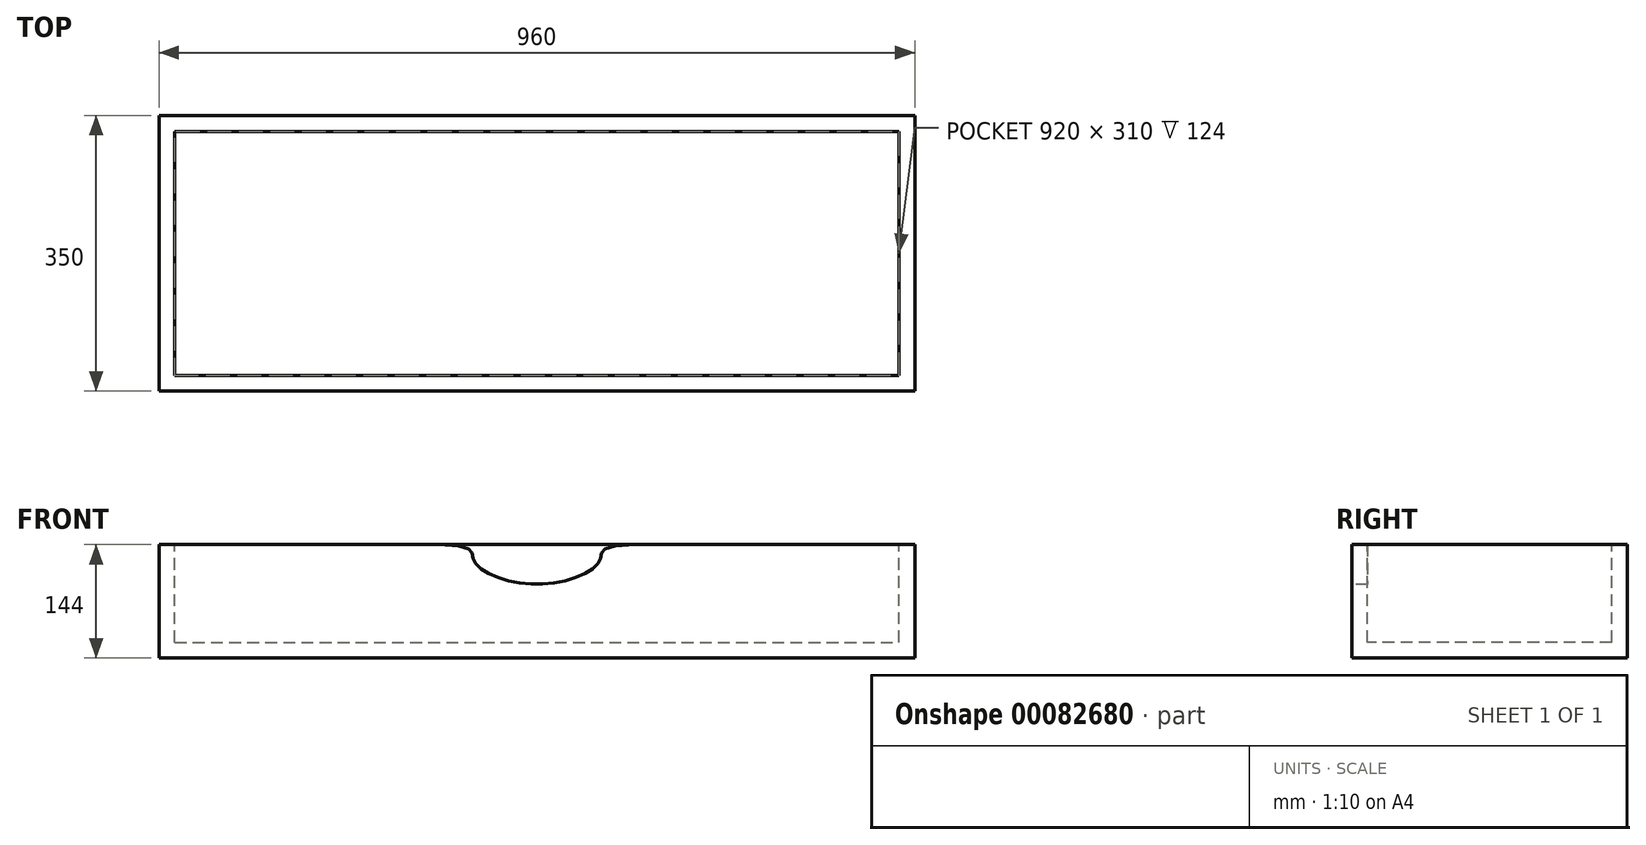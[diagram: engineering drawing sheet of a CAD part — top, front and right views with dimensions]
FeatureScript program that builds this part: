
annotation { "Feature Type Name" : "Feature", "Feature Type Description" : "" }
export const myFeature = defineFeature(function(context is Context, id is Id, definition is map)
    precondition{}
    {
        {
            var Q0;
            Q0=qCreatedBy(makeId("Top.planeOp"),FACE);
            var sketch = newSketch(context, id + "F0", { "sketchPlane" : qUnion([Q0])});
            skLineSegment(sketch, "E0.bottom", {"start": v(-480, 175) * mm, "end": v(480, 175) * mm});
            skLineSegment(sketch, "E0.top", {"start": v(-480, -175) * mm, "end": v(480, -175) * mm});
            skLineSegment(sketch, "E0.left", {"start": v(-480, 175) * mm, "end": v(-480, -175) * mm});
            skLineSegment(sketch, "E0.right", {"start": v(480, 175) * mm, "end": v(480, -175) * mm});
            skLineSegment(sketch, "E1", {"start": v(-480, 175) * mm, "end": v(480, -175) * mm, "construction": true});
            skSolve(sketch);
        }
        {
            var Q0;
            Q0 = qSketchRegion(id + "F0", true);
            extrude(context, id + "F1", {"entities" : qUnion([Q0]), "depth" : 144 * mm});
        }
        {
            var Q0;
            Q0=makeQuery(id+"F1.opExtrude","CAP_FACE",FACE,{"disambiguationData":[OSD([sQuery(id+"F0.wireOp",EDGE,"E0.bottom"),sQuery(id+"F0.wireOp",EDGE,"E0.top"),sQuery(id+"F0.wireOp",EDGE,"E0.left"),sQuery(id+"F0.wireOp",EDGE,"E0.right")])],"isStart":false});
            var sketch = newSketch(context, id + "F2", { "sketchPlane" : qUnion([Q0])});
            skLineSegment(sketch, "E2.bottom", {"start": v(-460, 155) * mm, "end": v(460, 155) * mm});
            skLineSegment(sketch, "E2.top", {"start": v(-460, -155) * mm, "end": v(460, -155) * mm});
            skLineSegment(sketch, "E2.left", {"start": v(-460, 155) * mm, "end": v(-460, -155) * mm});
            skLineSegment(sketch, "E2.right", {"start": v(460, 155) * mm, "end": v(460, -155) * mm});
            skSolve(sketch);
        }
        {
            var Q0;
            Q0 = qSketchRegion(id + "F2", true);
            extrude(context, id + "F3", {"entities" : qUnion([Q0]), "operationType" : NewBodyOperationType.REMOVE, "oppositeDirection" : true, "depth" : 124 * mm});
        }
        {
            var Q0;
            Q0=makeQuery(id+"F1.opExtrude","SWEPT_FACE",FACE,{"disambiguationData":[OSD([sQuery(id+"F0.wireOp",EDGE,"E0.top")])]});
            var sketch = newSketch(context, id + "F4", { "sketchPlane" : qUnion([Q0])});
            skLineSegment(sketch, "E3", {"start": v(-125, 144) * mm, "end": v(125, 144) * mm});
            skLineSegment(sketch, "E4", {"start": v(0, 144) * mm, "end": v(0, 54) * mm, "construction": true});
            skFitSpline(sketch, "E5", {"points": [v(-125, 144) * mm, v(-80, 124) * mm, v(-40, 99) * mm, v(40, 99) * mm, v(80, 124) * mm, v(125, 144) * mm], "startDerivative": vector(784.8, 0) * mm, "endDerivative": vector(784.8, 0) * mm});
            skLineSegment(sketch, "E6", {"start": v(75, 144) * mm, "end": v(-75, 144) * mm, "construction": true});
            skLineSegment(sketch, "E7", {"start": v(-80, 124) * mm, "end": v(80, 124) * mm, "construction": true});
            skLineSegment(sketch, "E8", {"start": v(-40, 99) * mm, "end": v(40, 99) * mm, "construction": true});
            skPoint(sketch, "E9", {"position": v(0, 124) * mm});
            skPoint(sketch, "E10", {"position": v(0, 99) * mm});
            skSolve(sketch);
        }
        {
            var Q0;
            Q0 = qSketchRegion(id + "F4", true);
            extrude(context, id + "F5", {"entities" : qUnion([Q0]), "operationType" : NewBodyOperationType.REMOVE, "oppositeDirection" : true, "depth" : 20 * mm});
        }
    });
